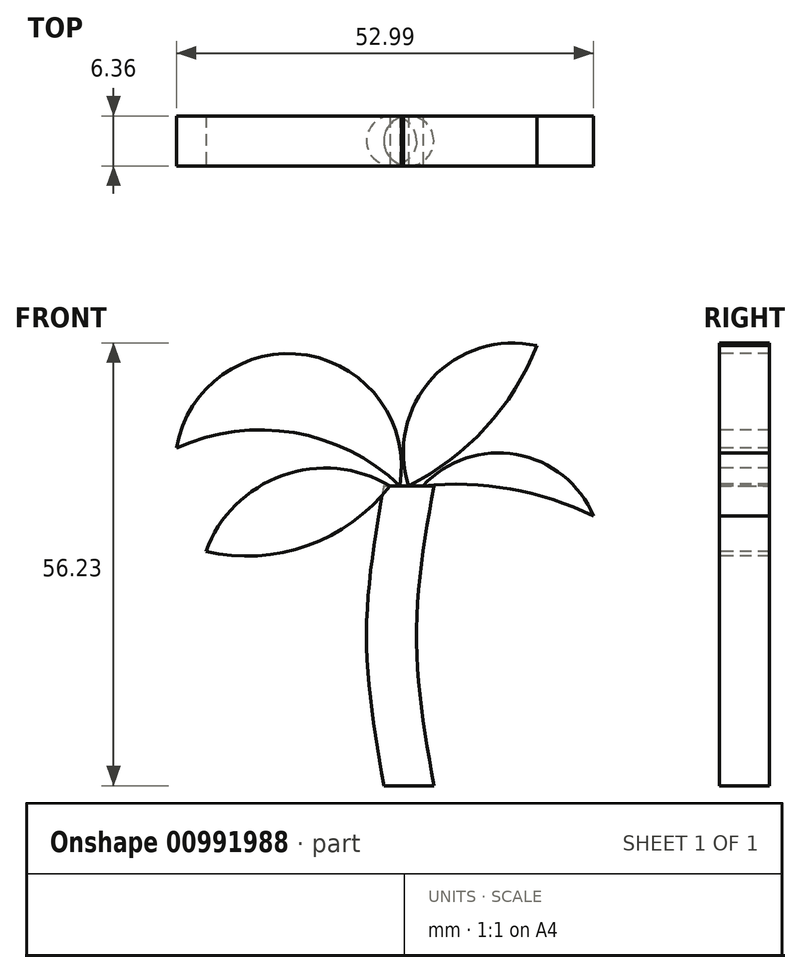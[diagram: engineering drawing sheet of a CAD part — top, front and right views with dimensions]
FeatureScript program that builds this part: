
annotation { "Feature Type Name" : "Feature", "Feature Type Description" : "" }
export const myFeature = defineFeature(function(context is Context, id is Id, definition is map)
    precondition{}
    {
        {
            var Q0;
            Q0=qCreatedBy(makeId("Top.planeOp"),FACE);
            var sketch = newSketch(context, id + "F0", { "sketchPlane" : qUnion([Q0])});
            skCircle(sketch, "E0", {"center": v(0, 0) * mm, "radius": 3.18 * mm});
            skSolve(sketch);
        }
        {
            var Q0;
            Q0=qCreatedBy(makeId("Top.planeOp"),FACE);
            cPlane(context, id + "F1", {"entities" : qUnion([Q0]), "cplaneType" : CPlaneType.OFFSET, "offset" : 19.05 * mm, "width" : 152.4 * mm, "height" : 152.4 * mm});
        }
        {
            var Q0;
            Q0=qCreatedBy(id+"F1.planeOp",FACE);
            cPlane(context, id + "F2", {"entities" : qUnion([Q0]), "cplaneType" : CPlaneType.OFFSET, "offset" : 19.05 * mm, "width" : 152.4 * mm, "height" : 152.4 * mm});
        }
        {
            var Q0;
            Q0=qCreatedBy(id+"F1.planeOp",FACE);
            var sketch = newSketch(context, id + "F3", { "sketchPlane" : qUnion([Q0])});
            skCircle(sketch, "E1", {"center": v(-2.2, 0) * mm, "radius": 3.18 * mm});
            skSolve(sketch);
        }
        {
            var Q0;
            Q0=qCreatedBy(id+"F2.planeOp",FACE);
            var sketch = newSketch(context, id + "F4", { "sketchPlane" : qUnion([Q0])});
            skCircle(sketch, "E2", {"center": v(0, 0) * mm, "radius": 3.18 * mm});
            skSolve(sketch);
        }
        {
            var Q0;
            Q0=makeQuery(id+"F0.imprint","IMPRINT",FACE,{"disambiguationData":[TD([[makeQuery(id+"F0.imprint","IMPRINT",EDGE,{"derivedFrom":sQuery(id+"F0.wireOp",EDGE,"E0")}),1.0]])]});
            var Q1;
            Q1=makeQuery(id+"F3.imprint","IMPRINT",FACE,{"disambiguationData":[TD([[makeQuery(id+"F3.imprint","IMPRINT",EDGE,{"derivedFrom":sQuery(id+"F3.wireOp",EDGE,"E1")}),1.0]])]});
            var Q2;
            Q2=makeQuery(id+"F4.imprint","IMPRINT",FACE,{"disambiguationData":[TD([[makeQuery(id+"F4.imprint","IMPRINT",EDGE,{"derivedFrom":sQuery(id+"F4.wireOp",EDGE,"E2")}),1.0]])]});
            loft(context, id + "F5", {"sheetProfilesArray" : [{ "sheetProfileEntities" : qUnion([Q0]) }, { "sheetProfileEntities" : qUnion([Q1]) }, { "sheetProfileEntities" : qUnion([Q2]) }]});
        }
        {
            var Q0;
            Q0=qCreatedBy(makeId("Front.planeOp"),FACE);
            cPlane(context, id + "F6", {"entities" : qUnion([Q0]), "cplaneType" : CPlaneType.OFFSET, "offset" : 3.17 * mm, "width" : 152.4 * mm, "height" : 152.4 * mm});
        }
        {
            var Q0;
            Q0=qCreatedBy(id+"F6.planeOp",FACE);
            var sketch = newSketch(context, id + "F7", { "sketchPlane" : qUnion([Q0])});
            skArc(sketch, "E3", {"start": v(-2.4, 38.1) * mm, "mid": v(-16.05, 39.4) * mm, "end": v(-25.77, 29.75) * mm});
            skArc(sketch, "E4", {"start": v(-1.13, 38.1) * mm, "mid": v(-12.92, 54.68) * mm, "end": v(-29.5, 42.88) * mm});
            skArc(sketch, "E5", {"start": v(23.49, 34.23) * mm, "mid": v(13.7, 42.06) * mm, "end": v(1.8, 38.1) * mm});
            skArc(sketch, "E6", {"start": v(16.27, 55.88) * mm, "mid": v(2.96, 51.73) * mm, "end": v(-0.02, 38.1) * mm});
            skArc(sketch, "E7", {"start": v(-1.13, 38.1) * mm, "mid": v(-14.58, 44.84) * mm, "end": v(-29.5, 42.88) * mm});
            skArc(sketch, "E8", {"start": v(-25.77, 29.75) * mm, "mid": v(-12.86, 30.49) * mm, "end": v(-2.4, 38.1) * mm});
            skArc(sketch, "E9", {"start": v(-0.02, 38.1) * mm, "mid": v(9.77, 45.49) * mm, "end": v(16.27, 55.88) * mm});
            skArc(sketch, "E10", {"start": v(23.49, 34.23) * mm, "mid": v(12.92, 37.69) * mm, "end": v(1.8, 38.1) * mm});
            skSolve(sketch);
        }
        {
            var Q0;
            Q0=makeQuery(id+"F7.imprint","IMPRINT",FACE,{"disambiguationData":[TD([[makeQuery(id+"F7.imprint","IMPRINT",EDGE,{"derivedFrom":sQuery(id+"F7.wireOp",EDGE,"E3")}),1.0]])]});
            var Q1;
            Q1=makeQuery(id+"F7.imprint","IMPRINT",FACE,{"disambiguationData":[TD([[makeQuery(id+"F7.imprint","IMPRINT",EDGE,{"derivedFrom":sQuery(id+"F7.wireOp",EDGE,"E4")}),1.0]])]});
            var Q2;
            Q2=makeQuery(id+"F7.imprint","IMPRINT",FACE,{"disambiguationData":[TD([[makeQuery(id+"F7.imprint","IMPRINT",EDGE,{"derivedFrom":sQuery(id+"F7.wireOp",EDGE,"E6")}),1.0]])]});
            var Q3;
            Q3=makeQuery(id+"F7.imprint","IMPRINT",FACE,{"disambiguationData":[TD([[makeQuery(id+"F7.imprint","IMPRINT",EDGE,{"derivedFrom":sQuery(id+"F7.wireOp",EDGE,"E5")}),1.0]])]});
            extrude(context, id + "F8", {"entities" : qUnion([Q0, Q1, Q2, Q3]), "oppositeDirection" : true, "depth" : 6.35 * mm, "offsetDistance" : 25.4 * mm});
        }
    });
